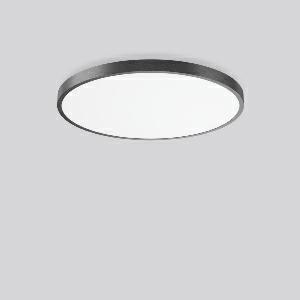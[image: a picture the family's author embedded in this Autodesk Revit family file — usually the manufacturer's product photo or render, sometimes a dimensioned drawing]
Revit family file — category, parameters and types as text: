
# Revit family: triona_round_a_312387_0031_1_76_6a00
name_source: partatom
category: Lighting Fixtures
units: mm (PartAtom-declared; Revit-internal decimal feet)

## family parameters
Cut with Voids When Loaded = No
Host = Face
Light Source = No
Part Type = Normal
Room Calculation Point = No
Round Connector Dimension = Use Diameter
Shared = No

## types (1)
- TRIONA round A (1 x LED Modul 840, 8300 lm, 4000)
    Apparent Load = 80 VA
    CIE Flux Codes = 49 80 96 100 100
    Color Rendering = 80
    Color Temperature = 4000
    Default Elevation = 1800 mm
    Description = Series: TRIONA round
Decorative round LED surface-mounted luminaire. Flat, seamless frame: aluminium extrusion profile, powder coated. Cover made of sheet steel, powder-coated. Light emission through a diffuser: plastic, opal. Lightguide and diffuser made of non-yellowing plastic (PMMA). Lateral light emission (RZB SIDELITE technology) for above-average homogeneous light distribution. Suitable for Ceiling mounting, Wall (surface). Tool-free mounting via bayonet connection. Electronic ballast included. Very easy installation thanks to Plug+Play connection. 
Colour: anthracite metallic (DB703)
Diameter: 845 mm
Height: 88 mm
Lamp: LED
Socket: without socket
Colour temperature: 4000K
Colour rendering index (CRI): 80
System power: 80 W
Rated luminous flux: 8300 lm
Luminous efficiency: 104 lm/W
Control gear: Converter, dimmable, DALI
Protection class: I
Type of protection: IP 20
    Height = 88 mm
    Lamp = 1 x LED Modul 840
    Lamp Light Flux = 8300 lm
    Lamp count = 1
    Length = 845 mm
    Lifetime = 50000 h
    Luminous efficacy = 104 lm/W
    Manufacturer = RZB
    ModVariant = No
    Model = 312387.0031.1.76
    Mounting Place = Ceiling
    Mounting Type = Surface mounted
    Number of Poles = 1
    OnlyDefault = Yes
    Power Factor = 1
    Product Name = TRIONA round A
    Product group = Surface mounted modular luminaires
    ProductGroupID = 306
    Protection Class = Protection class I
    Protection Degree = IP 20
    RLX_Detail_Level = 1
    RLX_Emergency_Light_Flux = 0 lm
    RLX_Emergency_Type = 0
    RLX_Emergency_Type_DB = No
    RlxData = <blob elided: 36217 chars, md5=976eb214>
    Socket = socket
    Standby Power = 0 W
    System Light Flux = 8300 lm
    System Power = 80 W
    Type Comments = Product without accessories
    Type Image = 312388.0031.jpg
    URL = http://relux.com
    VarID = ---
    Voltage = 230 V
    Voltage Range = 220-240 V
    Weight = 0.00 kg
    Width = 0 mm  [stored 0 ft]

note: [stored X ft] marks values corroborated as IEEE doubles in the binary element streams (Revit-internal decimal feet)

## geometry (parser evidence)
native form markers: Blend x4, Sweep x11
no freeform markers — native parametric forms only
